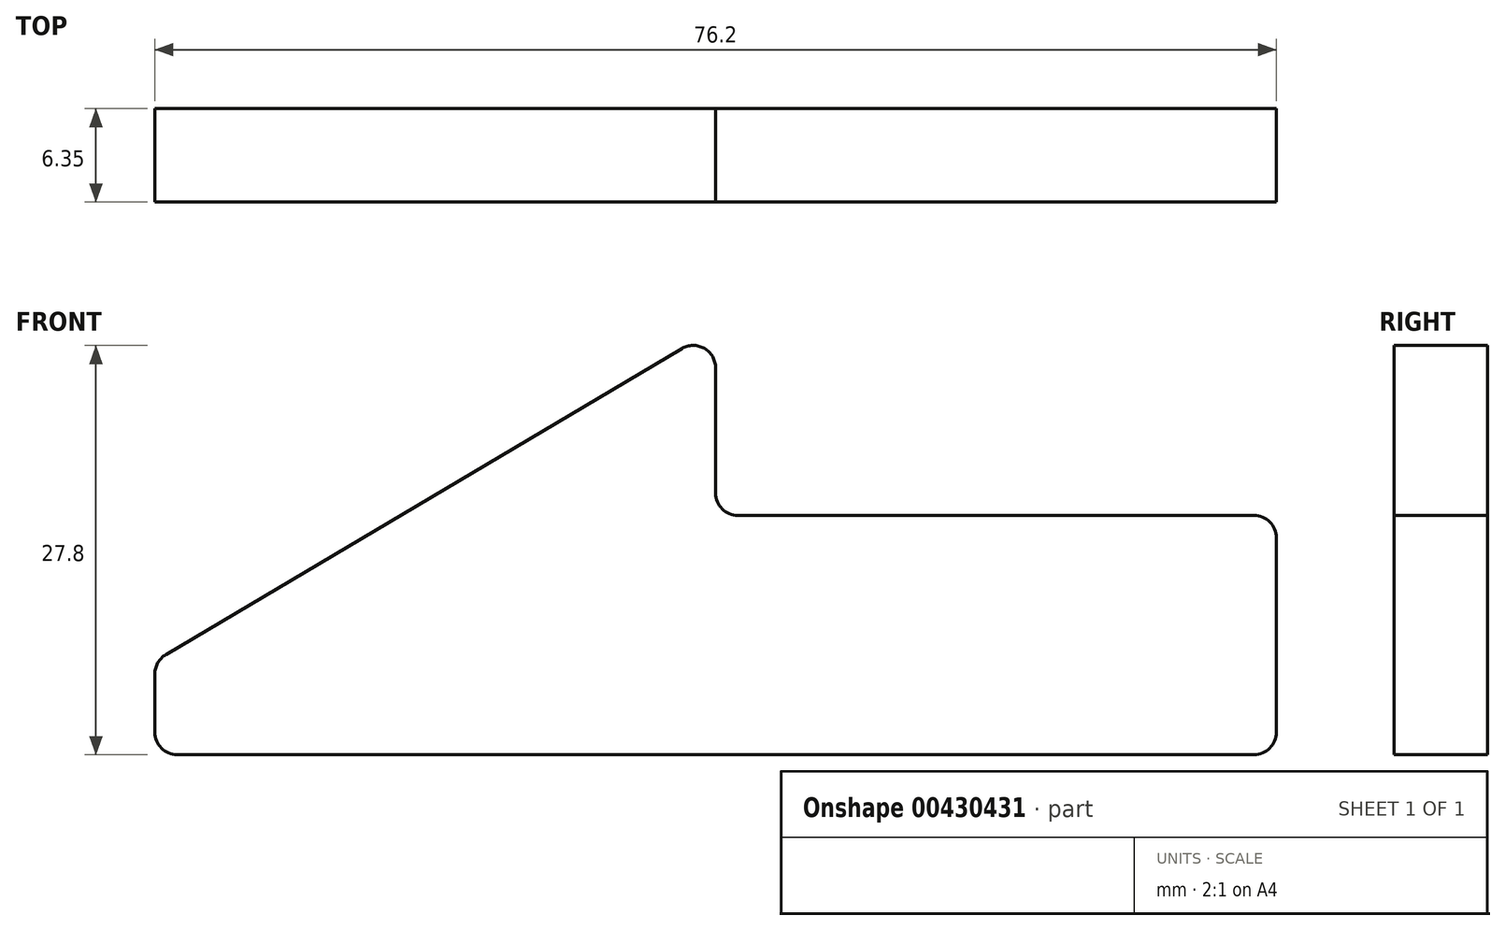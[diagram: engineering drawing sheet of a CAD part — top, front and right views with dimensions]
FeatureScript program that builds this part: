
annotation { "Feature Type Name" : "Feature", "Feature Type Description" : "" }
export const myFeature = defineFeature(function(context is Context, id is Id, definition is map)
    precondition{}
    {
        {
            var Q0;
            Q0=qCreatedBy(makeId("Front.planeOp"),FACE);
            var sketch = newSketch(context, id + "F0", { "sketchPlane" : qUnion([Q0])});
            skLineSegment(sketch, "E0", {"start": v(0, 22.6) * mm, "end": v(-38.1, 0) * mm});
            skLineSegment(sketch, "E1", {"start": v(-38.1, 0) * mm, "end": v(-38.1, -6.35) * mm});
            skLineSegment(sketch, "E2", {"start": v(-38.1, -6.35) * mm, "end": v(38.1, -6.35) * mm});
            skLineSegment(sketch, "E3", {"start": v(38.1, -6.35) * mm, "end": v(38.1, 9.9) * mm});
            skLineSegment(sketch, "E4", {"start": v(0, 22.6) * mm, "end": v(38.1, 22.6) * mm, "construction": true});
            skLineSegment(sketch, "E5", {"start": v(38.1, 9.9) * mm, "end": v(0, 9.9) * mm});
            skLineSegment(sketch, "E6", {"start": v(0, 9.9) * mm, "end": v(0, 22.6) * mm});
            skSolve(sketch);
        }
        {
            var Q0;
            Q0=makeQuery(id+"F0.imprint","IMPRINT",FACE,{"disambiguationData":[TD([[makeQuery(id+"F0.imprint","IMPRINT",EDGE,{"derivedFrom":sQuery(id+"F0.wireOp",EDGE,"E0")}),1.0]])]});
            extrude(context, id + "F1", {"entities" : qUnion([Q0]), "depth" : 6.35 * mm});
        }
        {
            var Q0;
            Q0=makeQuery(id+"F1.opExtrude","SWEPT_EDGE",EDGE,{"disambiguationData":[OSD([sQuery(id+"F0.wireOp",EDGE,"E0"),sQuery(id+"F0.wireOp",EDGE,"E6")])]});
            var Q1;
            Q1=makeQuery(id+"F1.opExtrude","SWEPT_EDGE",EDGE,{"disambiguationData":[OSD([sQuery(id+"F0.wireOp",EDGE,"E0"),sQuery(id+"F0.wireOp",EDGE,"E1")])]});
            var Q2;
            Q2=makeQuery(id+"F1.opExtrude","SWEPT_EDGE",EDGE,{"disambiguationData":[OSD([sQuery(id+"F0.wireOp",EDGE,"E1"),sQuery(id+"F0.wireOp",EDGE,"E2")])]});
            var Q3;
            Q3=makeQuery(id+"F1.opExtrude","SWEPT_EDGE",EDGE,{"disambiguationData":[OSD([sQuery(id+"F0.wireOp",EDGE,"E3"),sQuery(id+"F0.wireOp",EDGE,"E5")])]});
            var Q4;
            Q4=makeQuery(id+"F1.opExtrude","SWEPT_EDGE",EDGE,{"disambiguationData":[OSD([sQuery(id+"F0.wireOp",EDGE,"E2"),sQuery(id+"F0.wireOp",EDGE,"E3")])]});
            var Q5;
            Q5=makeQuery(id+"F1.opExtrude","SWEPT_EDGE",EDGE,{"disambiguationData":[OSD([sQuery(id+"F0.wireOp",EDGE,"E5"),sQuery(id+"F0.wireOp",EDGE,"E6")])]});
            fillet(context, id + "F2", {"entities" : qUnion([Q0, Q1, Q2, Q3, Q4, Q5]), "radius" : 1.52 * mm, "tangentPropagation" : true, "allowEdgeOverflow" : false});
        }
    });
